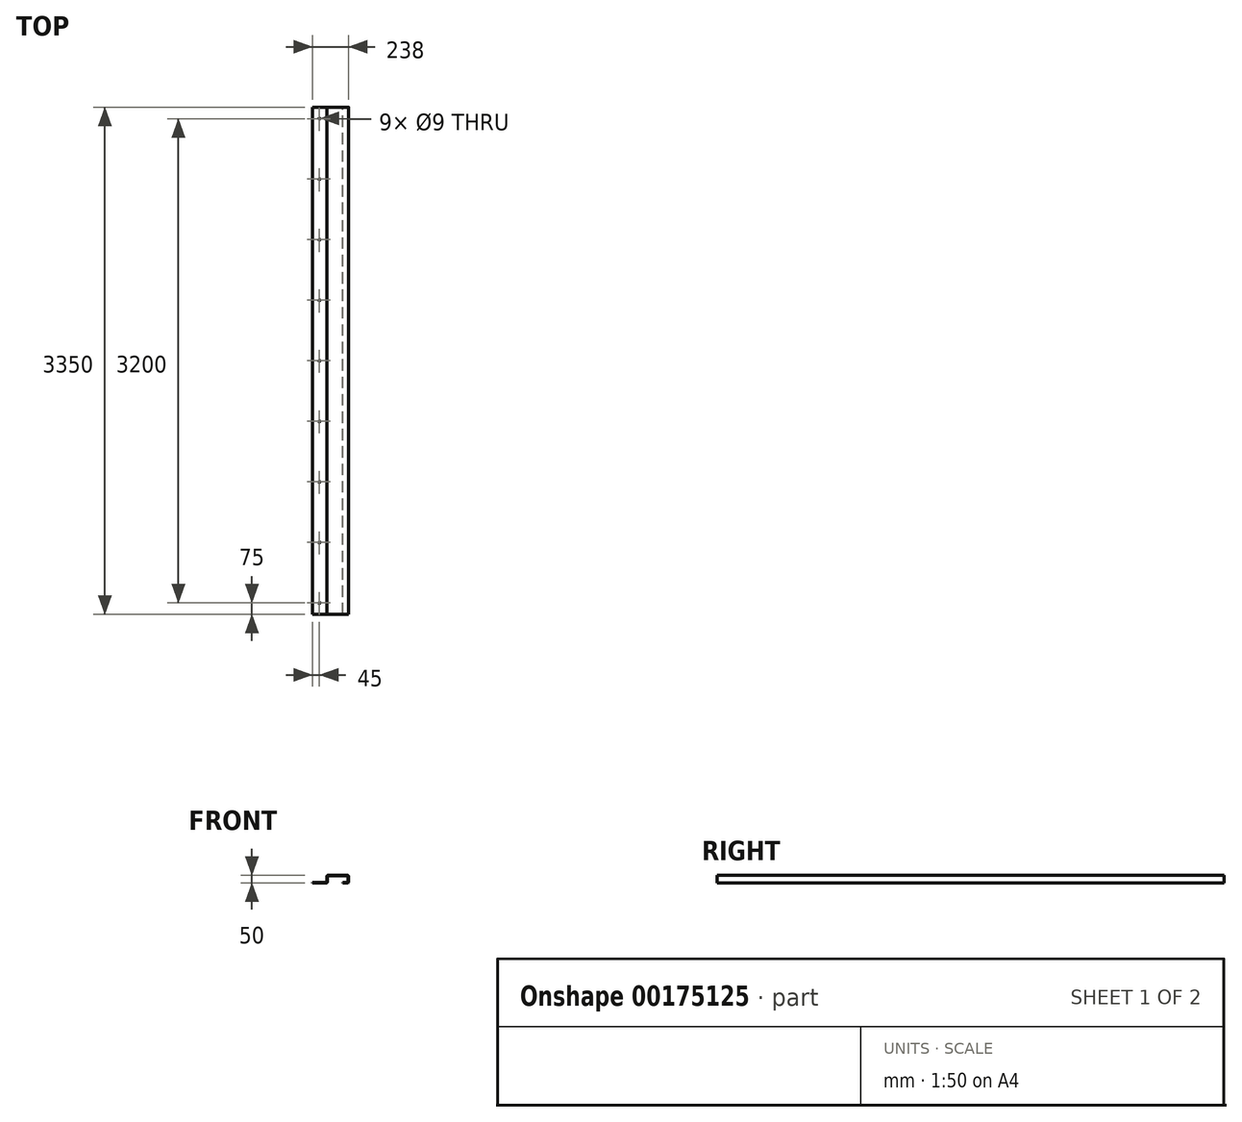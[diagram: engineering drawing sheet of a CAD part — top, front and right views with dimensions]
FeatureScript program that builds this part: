
annotation { "Feature Type Name" : "Feature", "Feature Type Description" : "" }
export const myFeature = defineFeature(function(context is Context, id is Id, definition is map)
    precondition{}
    {
        {
            var Q0;
            Q0=qCreatedBy(makeId("Front.planeOp"),FACE);
            var sketch = newSketch(context, id + "F0", { "sketchPlane" : qUnion([Q0])});
            skLineSegment(sketch, "E0", {"start": v(0, 0) * mm, "end": v(91, 0) * mm});
            skLineSegment(sketch, "E1", {"start": v(97, 6) * mm, "end": v(97, 44) * mm});
            skLineSegment(sketch, "E2", {"start": v(100, 47) * mm, "end": v(232, 47) * mm});
            skLineSegment(sketch, "E3.1", {"start": v(0, 3) * mm, "end": v(91, 3) * mm});
            skLineSegment(sketch, "E3.2", {"start": v(94, 6) * mm, "end": v(94, 44) * mm});
            skLineSegment(sketch, "E3.3", {"start": v(100, 50) * mm, "end": v(232, 50) * mm});
            skLineSegment(sketch, "E4", {"start": v(235, 44) * mm, "end": v(235, 6) * mm});
            skLineSegment(sketch, "E5", {"start": v(232, 3) * mm, "end": v(198, 3) * mm});
            skLineSegment(sketch, "E6", {"start": v(238, 44) * mm, "end": v(238, 6) * mm});
            skLineSegment(sketch, "E7", {"start": v(198, 3) * mm, "end": v(198, 0) * mm});
            skLineSegment(sketch, "E8", {"start": v(198, 0) * mm, "end": v(232, 0) * mm});
            skLineSegment(sketch, "E9", {"start": v(0, 3) * mm, "end": v(0, 0) * mm});
            skPoint(sketch, "E10.visualSharp", {"position": v(94, 3) * mm});
            skArc(sketch, "E10.filletArc", {"start": v(91, 3) * mm, "mid": v(93.12, 3.88) * mm, "end": v(94, 6) * mm});
            skPoint(sketch, "E11.visualSharp", {"position": v(97, 0) * mm});
            skArc(sketch, "E11.filletArc", {"start": v(91, 0) * mm, "mid": v(95.24, 1.76) * mm, "end": v(97, 6) * mm});
            skPoint(sketch, "E12.visualSharp", {"position": v(94, 50) * mm});
            skArc(sketch, "E12.filletArc", {"start": v(100, 50) * mm, "mid": v(95.76, 48.24) * mm, "end": v(94, 44) * mm});
            skPoint(sketch, "E13.visualSharp", {"position": v(97, 47) * mm});
            skArc(sketch, "E13.filletArc", {"start": v(100, 47) * mm, "mid": v(97.88, 46.12) * mm, "end": v(97, 44) * mm});
            skPoint(sketch, "E14.visualSharp", {"position": v(235, 47) * mm});
            skArc(sketch, "E14.filletArc", {"start": v(235, 44) * mm, "mid": v(234.12, 46.12) * mm, "end": v(232, 47) * mm});
            skPoint(sketch, "E15.visualSharp", {"position": v(238, 50) * mm});
            skArc(sketch, "E15.filletArc", {"start": v(238, 44) * mm, "mid": v(236.24, 48.24) * mm, "end": v(232, 50) * mm});
            skPoint(sketch, "E16.visualSharp", {"position": v(235, 3) * mm});
            skArc(sketch, "E16.filletArc", {"start": v(232, 3) * mm, "mid": v(234.12, 3.88) * mm, "end": v(235, 6) * mm});
            skPoint(sketch, "E17.visualSharp", {"position": v(238, 0) * mm});
            skArc(sketch, "E17.filletArc", {"start": v(232, 0) * mm, "mid": v(236.24, 1.76) * mm, "end": v(238, 6) * mm});
            skSolve(sketch);
        }
        {
            var Q0;
            Q0=makeQuery(id+"F0.imprint","IMPRINT",FACE,{"disambiguationData":[TD([[makeQuery(id+"F0.imprint","IMPRINT",EDGE,{"derivedFrom":sQuery(id+"F0.wireOp",EDGE,"E0")}),1.0]])]});
            extrude(context, id + "F1", {"entities" : qUnion([Q0]), "endBound" : BoundingType.SYMMETRIC, "depth" : 3350 * mm});
        }
        {
            var Q0;
            Q0=makeQuery(id+"F1.opExtrude","SWEPT_FACE",FACE,{"disambiguationData":[OSD([sQuery(id+"F0.wireOp",EDGE,"E3.1")])]});
            var sketch = newSketch(context, id + "F2", { "sketchPlane" : qUnion([Q0])});
            skLineSegment(sketch, "E18", {"start": v(0, 0) * mm, "end": v(90, 0) * mm});
            skCircle(sketch, "E19", {"center": v(45, 0) * mm, "radius": 4.5 * mm});
            skCircle(sketch, "E20.0.1.0", {"center": v(45, -400) * mm, "radius": 4.5 * mm});
            skCircle(sketch, "E20.0.2.0", {"center": v(45, -800) * mm, "radius": 4.5 * mm});
            skCircle(sketch, "E20.0.3.0", {"center": v(45, -1200) * mm, "radius": 4.5 * mm});
            skCircle(sketch, "E20.0.4.0", {"center": v(45, -1600) * mm, "radius": 4.5 * mm});
            skLineSegment(sketch, "E20.direction1", {"start": v(45, 0) * mm, "end": v(70, 0) * mm, "construction": true});
            skLineSegment(sketch, "E20.direction2", {"start": v(45, 0) * mm, "end": v(45, -400) * mm, "construction": true});
            skCircle(sketch, "E21.0.1.0", {"center": v(45, 400) * mm, "radius": 4.5 * mm});
            skLineSegment(sketch, "E21.0.1.1", {"start": v(45, 400) * mm, "end": v(45, 0) * mm, "construction": true});
            skCircle(sketch, "E21.0.2.0", {"center": v(45, 800) * mm, "radius": 4.5 * mm});
            skLineSegment(sketch, "E21.0.2.1", {"start": v(45, 800) * mm, "end": v(45, 400) * mm, "construction": true});
            skCircle(sketch, "E21.0.3.0", {"center": v(45, 1200) * mm, "radius": 4.5 * mm});
            skLineSegment(sketch, "E21.0.3.1", {"start": v(45, 1200) * mm, "end": v(45, 800) * mm, "construction": true});
            skLineSegment(sketch, "E21.direction2", {"start": v(45, 0) * mm, "end": v(45, 400) * mm, "construction": true});
            skCircle(sketch, "E22.0.0.4", {"center": v(45, 1600) * mm, "radius": 4.5 * mm});
            skLineSegment(sketch, "E22.2.0.4", {"start": v(45, 1600) * mm, "end": v(45, 1200) * mm, "construction": true});
            skSolve(sketch);
        }
        {
            var Q0;
            Q0 = qSketchRegion(id + "F2", true);
            var Q1;
            Q1=makeQuery(id+"F1.opExtrude","SWEPT_FACE",FACE,{"disambiguationData":[OSD([sQuery(id+"F0.wireOp",EDGE,"E0")])]});
            extrude(context, id + "F3", {"entities" : qUnion([Q0, Q1]), "operationType" : NewBodyOperationType.REMOVE, "oppositeDirection" : true, "depth" : 25 * mm});
        }
    });
